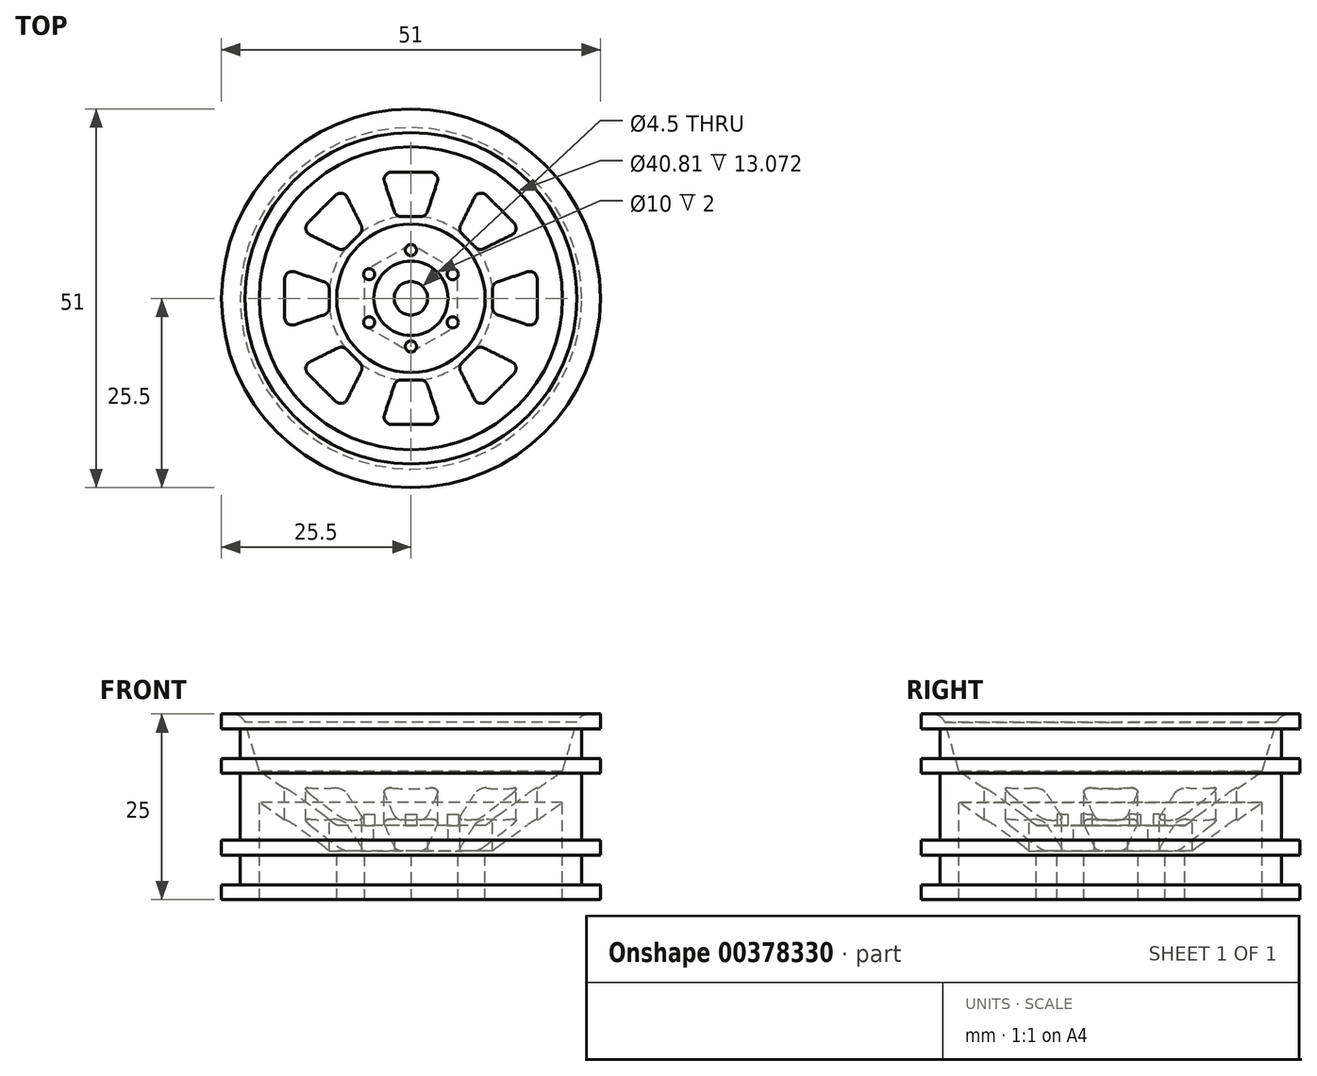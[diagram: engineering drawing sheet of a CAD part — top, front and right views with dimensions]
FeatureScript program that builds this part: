
annotation { "Feature Type Name" : "Feature", "Feature Type Description" : "" }
export const myFeature = defineFeature(function(context is Context, id is Id, definition is map)
    precondition{}
    {
        {
            var Q0;
            Q0=qCreatedBy(makeId("Front.planeOp"),FACE);
            var sketch = newSketch(context, id + "F0", { "sketchPlane" : qUnion([Q0])});
            skLineSegment(sketch, "E0", {"start": v(0, 0) * mm, "end": v(10.72, 0) * mm});
            skLineSegment(sketch, "E1", {"start": v(25.5, 0) * mm, "end": v(25.5, 2) * mm});
            skLineSegment(sketch, "E2", {"start": v(23, 2) * mm, "end": v(23, 6) * mm});
            skLineSegment(sketch, "E3", {"start": v(23, 2) * mm, "end": v(25.5, 2) * mm});
            skLineSegment(sketch, "E4", {"start": v(25.5, 6) * mm, "end": v(23, 6) * mm});
            skLineSegment(sketch, "E5", {"start": v(23, 8) * mm, "end": v(23, 17) * mm});
            skLineSegment(sketch, "E6", {"start": v(23.28, 23) * mm, "end": v(25.5, 23) * mm});
            skLineSegment(sketch, "E7", {"start": v(25.5, 23) * mm, "end": v(25.5, 25) * mm});
            skLineSegment(sketch, "E8", {"start": v(25.5, 25) * mm, "end": v(24.12, 25) * mm});
            skLineSegment(sketch, "E9", {"start": v(0, 10) * mm, "end": v(0, 0) * mm});
            skPoint(sketch, "E10.endSnap0", {"position": v(20, 25) * mm});
            skLineSegment(sketch, "E11", {"start": v(20.4, 17.29) * mm, "end": v(10, 10) * mm});
            skLineSegment(sketch, "E12", {"start": v(10, 10) * mm, "end": v(0, 10) * mm});
            skPoint(sketch, "E13.start.orphan", {"position": v(14.5, 25) * mm});
            skPoint(sketch, "E14.end.orphan", {"position": v(10.72, 0) * mm});
            skLineSegment(sketch, "E15.0", {"start": v(11.09, 6.55) * mm, "end": v(10, 6.55) * mm});
            skLineSegment(sketch, "E15.1", {"start": v(20.4, 13.07) * mm, "end": v(11.09, 6.55) * mm});
            skLineSegment(sketch, "E16", {"start": v(20.4, 13.07) * mm, "end": v(20.4, 0) * mm});
            skLineSegment(sketch, "E17", {"start": v(10, 6.55) * mm, "end": v(10, 0) * mm});
            skLineSegment(sketch, "E18.trimOffspring", {"start": v(20.4, 0) * mm, "end": v(25.5, 0) * mm});
            skLineSegment(sketch, "E19", {"start": v(25.5, 6) * mm, "end": v(25.5, 8) * mm});
            skLineSegment(sketch, "E20", {"start": v(25.5, 8) * mm, "end": v(23, 8) * mm});
            skPoint(sketch, "E21.end.orphan", {"position": v(23, 7.25) * mm});
            skPoint(sketch, "E22.end.orphan", {"position": v(26.5, 17) * mm});
            skPoint(sketch, "E23.end.orphan", {"position": v(25.5, 15) * mm});
            skLineSegment(sketch, "E24", {"start": v(23, 19) * mm, "end": v(25.5, 19) * mm});
            skLineSegment(sketch, "E25", {"start": v(25.5, 19) * mm, "end": v(25.5, 17) * mm});
            skLineSegment(sketch, "E26", {"start": v(25.5, 17) * mm, "end": v(23, 17) * mm});
            skLineSegment(sketch, "E27.trimOffspring", {"start": v(23, 19) * mm, "end": v(23, 22.72) * mm});
            skLineSegment(sketch, "E28.trimOffspring", {"start": v(23, 19) * mm, "end": v(23, 19) * mm});
            skPoint(sketch, "E29.visualSharp", {"position": v(20, 20.9) * mm});
            skPoint(sketch, "E30.visualSharp", {"position": v(22.5, 25) * mm});
            skArc(sketch, "E30.filletArc", {"start": v(24.12, 25) * mm, "mid": v(23.07, 24.7) * mm, "end": v(22.33, 23.9) * mm});
            skPoint(sketch, "E31.start.orphan", {"position": v(23, 19) * mm});
            skLineSegment(sketch, "E32", {"start": v(22.33, 23.9) * mm, "end": v(20.4, 17.29) * mm});
            skPoint(sketch, "E33.visualSharp", {"position": v(23, 23) * mm});
            skArc(sketch, "E33.filletArc", {"start": v(23.28, 23) * mm, "mid": v(23.08, 22.92) * mm, "end": v(23, 22.72) * mm});
            skPoint(sketch, "E34.orphan", {"position": v(0, 21) * mm});
            skSolve(sketch);
        }
        {
            var Q0;
            Q0=makeQuery(id+"F0.imprint","IMPRINT",FACE,{"disambiguationData":[TD([[makeQuery(id+"F0.imprint","IMPRINT",EDGE,{"derivedFrom":sQuery(id+"F0.wireOp",EDGE,"E1")}),1.0]])]});
            var Q1;
            Q1=sQuery(id+"F0.wireOp",EDGE,"E9");
            revolve(context, id + "F1", {"entities" : qUnion([Q0]), "axis" : qUnion([Q1]), "revolveType" : RevolveType.FULL});
        }
        {
            var Q0;
            Q0=makeQuery(id+"F1.opRevolve","SWEPT_FACE",FACE,{"disambiguationData":[OSD([sQuery(id+"F0.wireOp",EDGE,"E8")])]});
            cPlane(context, id + "F2", {"entities" : qUnion([Q0]), "cplaneType" : CPlaneType.OFFSET, "offset" : 25 * mm, "width" : 150 * mm, "height" : 150 * mm});
        }
        {
            var Q0;
            Q0=qCreatedBy(id+"F2.planeOp",FACE);
            var sketch = newSketch(context, id + "F3", { "sketchPlane" : qUnion([Q0])});
            skLineSegment(sketch, "E35", {"start": v(-2.61, 17) * mm, "end": v(2.61, 17) * mm});
            skLineSegment(sketch, "E36", {"start": v(3.56, 15.68) * mm, "end": v(2.23, 11.68) * mm});
            skLineSegment(sketch, "E37", {"start": v(1.28, 11) * mm, "end": v(-1.28, 11) * mm});
            skLineSegment(sketch, "E38", {"start": v(-2.23, 11.68) * mm, "end": v(-3.56, 15.68) * mm});
            skPoint(sketch, "E39.visualSharp", {"position": v(-4, 17) * mm});
            skArc(sketch, "E39.filletArc", {"start": v(-2.61, 17) * mm, "mid": v(-3.42, 16.58) * mm, "end": v(-3.56, 15.68) * mm});
            skPoint(sketch, "E40.visualSharp", {"position": v(-2, 11) * mm});
            skArc(sketch, "E40.filletArc", {"start": v(-2.23, 11.68) * mm, "mid": v(-1.86, 11.19) * mm, "end": v(-1.28, 11) * mm});
            skPoint(sketch, "E41.visualSharp", {"position": v(2, 11) * mm});
            skArc(sketch, "E41.filletArc", {"start": v(1.28, 11) * mm, "mid": v(1.86, 11.19) * mm, "end": v(2.23, 11.68) * mm});
            skPoint(sketch, "E42.visualSharp", {"position": v(4, 17) * mm});
            skArc(sketch, "E42.filletArc", {"start": v(3.56, 15.68) * mm, "mid": v(3.42, 16.58) * mm, "end": v(2.61, 17) * mm});
            skLineSegment(sketch, "E43.1.0", {"start": v(-9.84, 6.69) * mm, "end": v(-13.6, 8.57) * mm});
            skLineSegment(sketch, "E43.1.1", {"start": v(-13.87, 10.17) * mm, "end": v(-10.17, 13.87) * mm});
            skLineSegment(sketch, "E43.1.2", {"start": v(-8.57, 13.6) * mm, "end": v(-6.69, 9.84) * mm});
            skLineSegment(sketch, "E43.1.3", {"start": v(-6.87, 8.68) * mm, "end": v(-8.68, 6.87) * mm});
            skArc(sketch, "E43.1.4", {"start": v(-6.87, 8.68) * mm, "mid": v(-6.6, 9.23) * mm, "end": v(-6.69, 9.84) * mm});
            skArc(sketch, "E43.1.5", {"start": v(-9.84, 6.69) * mm, "mid": v(-9.23, 6.6) * mm, "end": v(-8.68, 6.87) * mm});
            skArc(sketch, "E43.1.6", {"start": v(-8.57, 13.6) * mm, "mid": v(-9.3, 14.15) * mm, "end": v(-10.17, 13.87) * mm});
            skArc(sketch, "E43.1.7", {"start": v(-13.87, 10.17) * mm, "mid": v(-14.15, 9.3) * mm, "end": v(-13.6, 8.57) * mm});
            skLineSegment(sketch, "E43.2.0", {"start": v(-11.68, -2.23) * mm, "end": v(-15.68, -3.56) * mm});
            skLineSegment(sketch, "E43.2.1", {"start": v(-17, -2.61) * mm, "end": v(-17, 2.61) * mm});
            skLineSegment(sketch, "E43.2.2", {"start": v(-15.68, 3.56) * mm, "end": v(-11.68, 2.23) * mm});
            skLineSegment(sketch, "E43.2.3", {"start": v(-11, 1.28) * mm, "end": v(-11, -1.28) * mm});
            skArc(sketch, "E43.2.4", {"start": v(-11, 1.28) * mm, "mid": v(-11.19, 1.86) * mm, "end": v(-11.68, 2.23) * mm});
            skArc(sketch, "E43.2.5", {"start": v(-11.68, -2.23) * mm, "mid": v(-11.19, -1.86) * mm, "end": v(-11, -1.28) * mm});
            skArc(sketch, "E43.2.6", {"start": v(-15.68, 3.56) * mm, "mid": v(-16.58, 3.42) * mm, "end": v(-17, 2.61) * mm});
            skArc(sketch, "E43.2.7", {"start": v(-17, -2.61) * mm, "mid": v(-16.58, -3.42) * mm, "end": v(-15.68, -3.56) * mm});
            skLineSegment(sketch, "E43.3.0", {"start": v(-6.69, -9.84) * mm, "end": v(-8.57, -13.6) * mm});
            skLineSegment(sketch, "E43.3.1", {"start": v(-10.17, -13.87) * mm, "end": v(-13.87, -10.17) * mm});
            skLineSegment(sketch, "E43.3.2", {"start": v(-13.6, -8.57) * mm, "end": v(-9.84, -6.69) * mm});
            skLineSegment(sketch, "E43.3.3", {"start": v(-8.68, -6.87) * mm, "end": v(-6.87, -8.68) * mm});
            skArc(sketch, "E43.3.4", {"start": v(-8.68, -6.87) * mm, "mid": v(-9.23, -6.6) * mm, "end": v(-9.84, -6.69) * mm});
            skArc(sketch, "E43.3.5", {"start": v(-6.69, -9.84) * mm, "mid": v(-6.6, -9.23) * mm, "end": v(-6.87, -8.68) * mm});
            skArc(sketch, "E43.3.6", {"start": v(-13.6, -8.57) * mm, "mid": v(-14.15, -9.3) * mm, "end": v(-13.87, -10.17) * mm});
            skArc(sketch, "E43.3.7", {"start": v(-10.17, -13.87) * mm, "mid": v(-9.3, -14.15) * mm, "end": v(-8.57, -13.6) * mm});
            skLineSegment(sketch, "E43.4.0", {"start": v(2.23, -11.68) * mm, "end": v(3.56, -15.68) * mm});
            skLineSegment(sketch, "E43.4.1", {"start": v(2.61, -17) * mm, "end": v(-2.61, -17) * mm});
            skLineSegment(sketch, "E43.4.2", {"start": v(-3.56, -15.68) * mm, "end": v(-2.23, -11.68) * mm});
            skLineSegment(sketch, "E43.4.3", {"start": v(-1.28, -11) * mm, "end": v(1.28, -11) * mm});
            skArc(sketch, "E43.4.4", {"start": v(-1.28, -11) * mm, "mid": v(-1.86, -11.19) * mm, "end": v(-2.23, -11.68) * mm});
            skArc(sketch, "E43.4.5", {"start": v(2.23, -11.68) * mm, "mid": v(1.86, -11.19) * mm, "end": v(1.28, -11) * mm});
            skArc(sketch, "E43.4.6", {"start": v(-3.56, -15.68) * mm, "mid": v(-3.42, -16.58) * mm, "end": v(-2.61, -17) * mm});
            skArc(sketch, "E43.4.7", {"start": v(2.61, -17) * mm, "mid": v(3.42, -16.58) * mm, "end": v(3.56, -15.68) * mm});
            skLineSegment(sketch, "E43.5.0", {"start": v(9.84, -6.69) * mm, "end": v(13.6, -8.57) * mm});
            skLineSegment(sketch, "E43.5.1", {"start": v(13.87, -10.17) * mm, "end": v(10.17, -13.87) * mm});
            skLineSegment(sketch, "E43.5.2", {"start": v(8.57, -13.6) * mm, "end": v(6.69, -9.84) * mm});
            skLineSegment(sketch, "E43.5.3", {"start": v(6.87, -8.68) * mm, "end": v(8.68, -6.87) * mm});
            skArc(sketch, "E43.5.4", {"start": v(6.87, -8.68) * mm, "mid": v(6.6, -9.23) * mm, "end": v(6.69, -9.84) * mm});
            skArc(sketch, "E43.5.5", {"start": v(9.84, -6.69) * mm, "mid": v(9.23, -6.6) * mm, "end": v(8.68, -6.87) * mm});
            skArc(sketch, "E43.5.6", {"start": v(8.57, -13.6) * mm, "mid": v(9.3, -14.15) * mm, "end": v(10.17, -13.87) * mm});
            skArc(sketch, "E43.5.7", {"start": v(13.87, -10.17) * mm, "mid": v(14.15, -9.3) * mm, "end": v(13.6, -8.57) * mm});
            skLineSegment(sketch, "E43.6.0", {"start": v(11.68, 2.23) * mm, "end": v(15.68, 3.56) * mm});
            skLineSegment(sketch, "E43.6.1", {"start": v(17, 2.61) * mm, "end": v(17, -2.61) * mm});
            skLineSegment(sketch, "E43.6.2", {"start": v(15.68, -3.56) * mm, "end": v(11.68, -2.23) * mm});
            skLineSegment(sketch, "E43.6.3", {"start": v(11, -1.28) * mm, "end": v(11, 1.28) * mm});
            skArc(sketch, "E43.6.4", {"start": v(11, -1.28) * mm, "mid": v(11.19, -1.86) * mm, "end": v(11.68, -2.23) * mm});
            skArc(sketch, "E43.6.5", {"start": v(11.68, 2.23) * mm, "mid": v(11.19, 1.86) * mm, "end": v(11, 1.28) * mm});
            skArc(sketch, "E43.6.6", {"start": v(15.68, -3.56) * mm, "mid": v(16.58, -3.42) * mm, "end": v(17, -2.61) * mm});
            skArc(sketch, "E43.6.7", {"start": v(17, 2.61) * mm, "mid": v(16.58, 3.42) * mm, "end": v(15.68, 3.56) * mm});
            skLineSegment(sketch, "E43.7.0", {"start": v(6.69, 9.84) * mm, "end": v(8.57, 13.6) * mm});
            skLineSegment(sketch, "E43.7.1", {"start": v(10.17, 13.87) * mm, "end": v(13.87, 10.17) * mm});
            skLineSegment(sketch, "E43.7.2", {"start": v(13.6, 8.57) * mm, "end": v(9.84, 6.69) * mm});
            skLineSegment(sketch, "E43.7.3", {"start": v(8.68, 6.87) * mm, "end": v(6.87, 8.68) * mm});
            skArc(sketch, "E43.7.4", {"start": v(8.68, 6.87) * mm, "mid": v(9.23, 6.6) * mm, "end": v(9.84, 6.69) * mm});
            skArc(sketch, "E43.7.5", {"start": v(6.69, 9.84) * mm, "mid": v(6.6, 9.23) * mm, "end": v(6.87, 8.68) * mm});
            skArc(sketch, "E43.7.6", {"start": v(13.6, 8.57) * mm, "mid": v(14.15, 9.3) * mm, "end": v(13.87, 10.17) * mm});
            skArc(sketch, "E43.7.7", {"start": v(10.17, 13.87) * mm, "mid": v(9.3, 14.15) * mm, "end": v(8.57, 13.6) * mm});
            skPoint(sketch, "E43.center", {"position": v(0, 0) * mm});
            skSolve(sketch);
        }
        {
            var Q0;
            Q0=makeQuery(id+"F3.imprint","IMPRINT",FACE,{"disambiguationData":[TD([[makeQuery(id+"F3.imprint","IMPRINT",EDGE,{"derivedFrom":sQuery(id+"F3.wireOp",EDGE,"E35")}),-1.0]])]});
            var Q1;
            Q1=makeQuery(id+"F3.imprint","IMPRINT",FACE,{"disambiguationData":[TD([[makeQuery(id+"F3.imprint","IMPRINT",EDGE,{"derivedFrom":sQuery(id+"F3.wireOp",EDGE,"E43.1.0")}),-1.0]])]});
            var Q2;
            Q2=makeQuery(id+"F3.imprint","IMPRINT",FACE,{"disambiguationData":[TD([[makeQuery(id+"F3.imprint","IMPRINT",EDGE,{"derivedFrom":sQuery(id+"F3.wireOp",EDGE,"E43.2.0")}),-1.0]])]});
            var Q3;
            Q3=makeQuery(id+"F3.imprint","IMPRINT",FACE,{"disambiguationData":[TD([[makeQuery(id+"F3.imprint","IMPRINT",EDGE,{"derivedFrom":sQuery(id+"F3.wireOp",EDGE,"E43.3.0")}),-1.0]])]});
            var Q4;
            Q4=makeQuery(id+"F3.imprint","IMPRINT",FACE,{"disambiguationData":[TD([[makeQuery(id+"F3.imprint","IMPRINT",EDGE,{"derivedFrom":sQuery(id+"F3.wireOp",EDGE,"E43.4.0")}),-1.0]])]});
            var Q5;
            Q5=makeQuery(id+"F3.imprint","IMPRINT",FACE,{"disambiguationData":[TD([[makeQuery(id+"F3.imprint","IMPRINT",EDGE,{"derivedFrom":sQuery(id+"F3.wireOp",EDGE,"E43.5.0")}),-1.0]])]});
            var Q6;
            Q6=makeQuery(id+"F3.imprint","IMPRINT",FACE,{"disambiguationData":[TD([[makeQuery(id+"F3.imprint","IMPRINT",EDGE,{"derivedFrom":sQuery(id+"F3.wireOp",EDGE,"E43.6.0")}),-1.0]])]});
            var Q7;
            Q7=makeQuery(id+"F3.imprint","IMPRINT",FACE,{"disambiguationData":[TD([[makeQuery(id+"F3.imprint","IMPRINT",EDGE,{"derivedFrom":sQuery(id+"F3.wireOp",EDGE,"E43.7.0")}),-1.0]])]});
            extrude(context, id + "F4", {"entities" : qUnion([Q0, Q1, Q2, Q3, Q4, Q5, Q6, Q7]), "operationType" : NewBodyOperationType.REMOVE, "endBound" : BoundingType.THROUGH_ALL, "oppositeDirection" : true, "depth" : 25 * mm});
        }
        {
            var Q0;
            Q0=makeQuery(id+"F1.opRevolve","SWEPT_FACE",FACE,{"disambiguationData":[OSD([sQuery(id+"F0.wireOp",EDGE,"E12")])]});
            var sketch = newSketch(context, id + "F5", { "sketchPlane" : qUnion([Q0])});
            skCircle(sketch, "E44", {"center": v(0, 6.5) * mm, "radius": 0.75 * mm});
            skCircle(sketch, "E45.1.0", {"center": v(-5.63, 3.25) * mm, "radius": 0.75 * mm});
            skCircle(sketch, "E45.2.0", {"center": v(-5.63, -3.25) * mm, "radius": 0.75 * mm});
            skCircle(sketch, "E45.3.0", {"center": v(0, -6.5) * mm, "radius": 0.75 * mm});
            skCircle(sketch, "E45.4.0", {"center": v(5.63, -3.25) * mm, "radius": 0.75 * mm});
            skCircle(sketch, "E45.5.0", {"center": v(5.63, 3.25) * mm, "radius": 0.75 * mm});
            skPoint(sketch, "E45.center", {"position": v(0, 0) * mm});
            skSolve(sketch);
        }
        {
            var Q0;
            Q0=makeQuery(id+"F5.imprint","IMPRINT",FACE,{"disambiguationData":[TD([[makeQuery(id+"F5.imprint","IMPRINT",EDGE,{"derivedFrom":sQuery(id+"F5.wireOp",EDGE,"E44")}),1.0]])]});
            var Q1;
            Q1=makeQuery(id+"F5.imprint","IMPRINT",FACE,{"disambiguationData":[TD([[makeQuery(id+"F5.imprint","IMPRINT",EDGE,{"derivedFrom":sQuery(id+"F5.wireOp",EDGE,"E45.1.0")}),1.0]])]});
            var Q2;
            Q2=makeQuery(id+"F5.imprint","IMPRINT",FACE,{"disambiguationData":[TD([[makeQuery(id+"F5.imprint","IMPRINT",EDGE,{"derivedFrom":sQuery(id+"F5.wireOp",EDGE,"E45.2.0")}),1.0]])]});
            var Q3;
            Q3=makeQuery(id+"F5.imprint","IMPRINT",FACE,{"disambiguationData":[TD([[makeQuery(id+"F5.imprint","IMPRINT",EDGE,{"derivedFrom":sQuery(id+"F5.wireOp",EDGE,"E45.3.0")}),1.0]])]});
            var Q4;
            Q4=makeQuery(id+"F5.imprint","IMPRINT",FACE,{"disambiguationData":[TD([[makeQuery(id+"F5.imprint","IMPRINT",EDGE,{"derivedFrom":sQuery(id+"F5.wireOp",EDGE,"E45.4.0")}),1.0]])]});
            var Q5;
            Q5=makeQuery(id+"F5.imprint","IMPRINT",FACE,{"disambiguationData":[TD([[makeQuery(id+"F5.imprint","IMPRINT",EDGE,{"derivedFrom":sQuery(id+"F5.wireOp",EDGE,"E45.5.0")}),1.0]])]});
            extrude(context, id + "F6", {"entities" : qUnion([Q0, Q1, Q2, Q3, Q4, Q5]), "operationType" : NewBodyOperationType.ADD, "depth" : 1.5 * mm});
        }
        {
            var Q0;
            Q0=makeQuery(id+"F1.opRevolve","SWEPT_FACE",FACE,{"disambiguationData":[OSD([sQuery(id+"F0.wireOp",EDGE,"E0")])]});
            var sketch = newSketch(context, id + "F7", { "sketchPlane" : qUnion([Q0])});
            skCircle(sketch, "E46.cCircle", {"center": v(0, 0) * mm, "radius": 6.3 * mm, "construction": true});
            skLineSegment(sketch, "E46.0", {"start": v(6.3, -3.64) * mm, "end": v(0, -7.27) * mm});
            skLineSegment(sketch, "E46.1", {"start": v(0, -7.27) * mm, "end": v(-6.3, -3.64) * mm});
            skLineSegment(sketch, "E46.2", {"start": v(-6.3, -3.64) * mm, "end": v(-6.3, 3.64) * mm});
            skLineSegment(sketch, "E46.3", {"start": v(-6.3, 3.64) * mm, "end": v(0, 7.27) * mm});
            skLineSegment(sketch, "E46.4", {"start": v(0, 7.27) * mm, "end": v(6.3, 3.64) * mm});
            skLineSegment(sketch, "E46.5", {"start": v(6.3, 3.64) * mm, "end": v(6.3, -3.64) * mm});
            skPoint(sketch, "E46.0.midPoint", {"position": v(3.15, -5.46) * mm});
            skSolve(sketch);
        }
        {
            var Q0;
            Q0=makeQuery(id+"F7.imprint","IMPRINT",FACE,{"disambiguationData":[TD([[makeQuery(id+"F7.imprint","IMPRINT",EDGE,{"derivedFrom":sQuery(id+"F7.wireOp",EDGE,"E46.0")}),-1.0]])]});
            extrude(context, id + "F8", {"entities" : qUnion([Q0]), "operationType" : NewBodyOperationType.REMOVE, "oppositeDirection" : true, "depth" : 6 * mm});
        }
        {
            var Q0;
            Q0=makeQuery(id+"F8.boolean.opBoolean","COPY",FACE,{"derivedFrom":makeQuery(id+"F8.opExtrude","CAP_FACE",FACE,{"disambiguationData":[OSD([sQuery(id+"F7.wireOp",EDGE,"E46.0"),sQuery(id+"F7.wireOp",EDGE,"E46.1"),sQuery(id+"F7.wireOp",EDGE,"E46.2"),sQuery(id+"F7.wireOp",EDGE,"E46.3"),sQuery(id+"F7.wireOp",EDGE,"E46.4"),sQuery(id+"F7.wireOp",EDGE,"E46.5")])],"isStart":false})});
            var sketch = newSketch(context, id + "F9", { "sketchPlane" : qUnion([Q0])});
            skCircle(sketch, "E47", {"center": v(0, 0) * mm, "radius": 2.25 * mm});
            skSolve(sketch);
        }
        {
            var Q0;
            Q0=makeQuery(id+"F9.imprint","IMPRINT",FACE,{"disambiguationData":[TD([[makeQuery(id+"F9.imprint","IMPRINT",EDGE,{"derivedFrom":sQuery(id+"F9.wireOp",EDGE,"E47")}),1.0]])]});
            extrude(context, id + "F10", {"entities" : qUnion([Q0]), "operationType" : NewBodyOperationType.ADD, "depth" : 25 * mm});
        }
        {
            var Q0;
            Q0=makeQuery(id+"F10.opExtrude","CAP_FACE",FACE,{"disambiguationData":[OSD([sQuery(id+"F9.wireOp",EDGE,"E47")])],"isStart":false});
            extrude(context, id + "F11", {"entities" : qUnion([Q0]), "operationType" : NewBodyOperationType.REMOVE, "endBound" : BoundingType.THROUGH_ALL, "oppositeDirection" : true, "depth" : 25 * mm});
        }
        {
            var Q0;
            Q0=makeQuery(id+"F1.opRevolve","SWEPT_FACE",FACE,{"disambiguationData":[OSD([sQuery(id+"F0.wireOp",EDGE,"E12")])]});
            var sketch = newSketch(context, id + "F12", { "sketchPlane" : qUnion([Q0])});
            skCircle(sketch, "E48", {"center": v(0, 0) * mm, "radius": 5 * mm});
            skSolve(sketch);
        }
        {
            var Q0;
            Q0=makeQuery(id+"F12.imprint","IMPRINT",FACE,{"disambiguationData":[TD([[makeQuery(id+"F12.imprint","IMPRINT",EDGE,{"derivedFrom":sQuery(id+"F12.wireOp",EDGE,"E48")}),1.0]])]});
            extrude(context, id + "F13", {"entities" : qUnion([Q0]), "operationType" : NewBodyOperationType.REMOVE, "oppositeDirection" : true, "depth" : 2 * mm});
        }
    });
